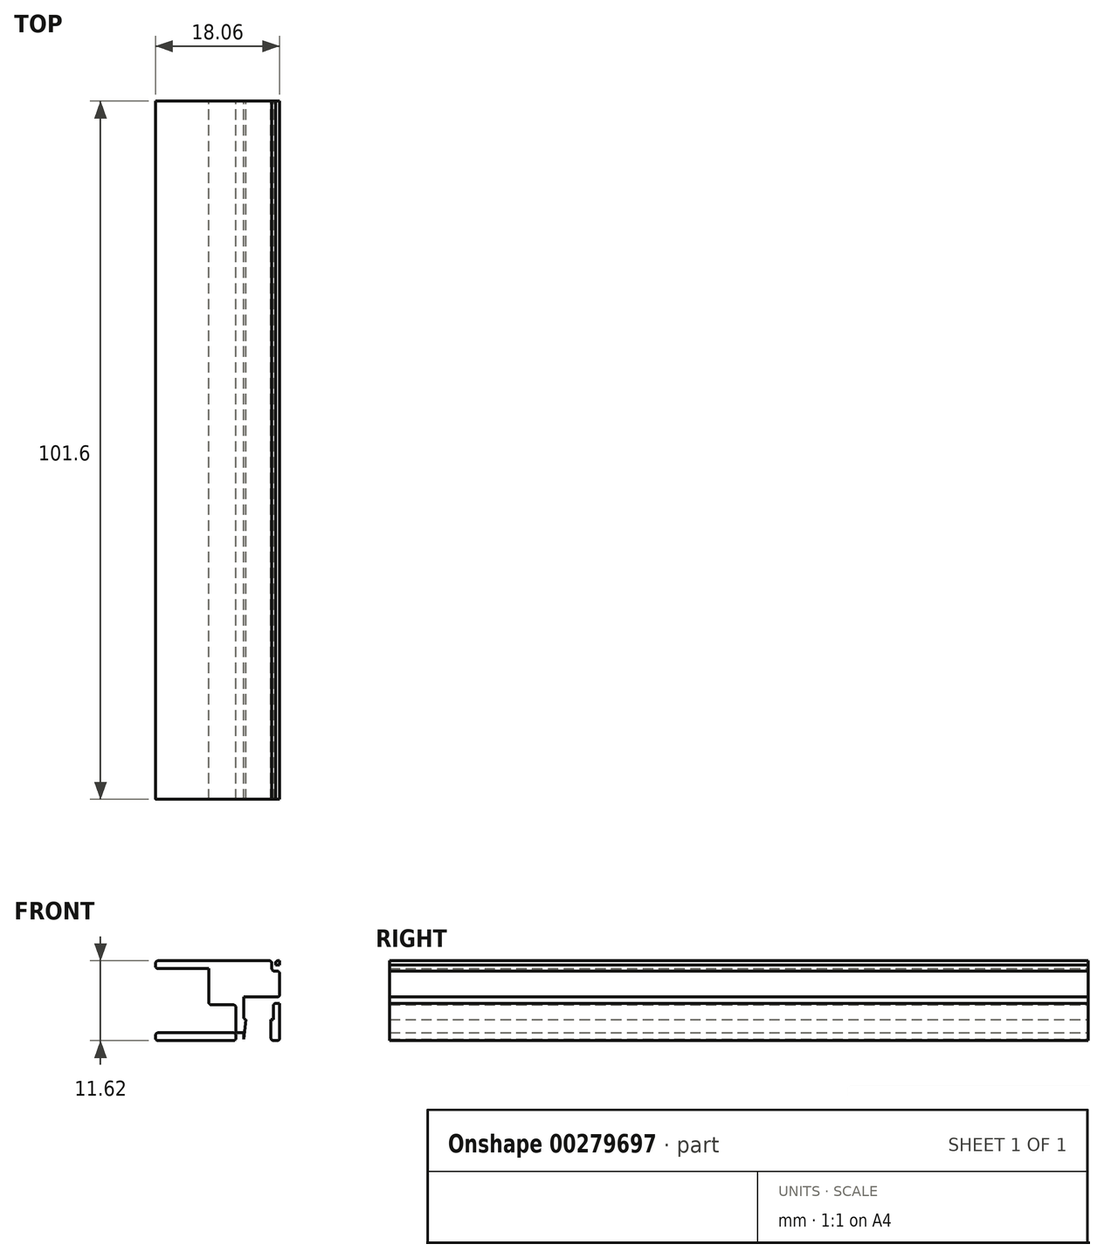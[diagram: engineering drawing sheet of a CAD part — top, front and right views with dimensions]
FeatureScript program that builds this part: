
annotation { "Feature Type Name" : "Feature", "Feature Type Description" : "" }
export const myFeature = defineFeature(function(context is Context, id is Id, definition is map)
    precondition{}
    {
        {
            var Q0;
            Q0=qCreatedBy(makeId("Front.planeOp"),FACE);
            var sketch = newSketch(context, id + "F0", { "sketchPlane" : qUnion([Q0])});
            skLineSegment(sketch, "E0.bottom", {"start": v(12.78, 5.81) * mm, "end": v(-12.78, 5.81) * mm});
            skLineSegment(sketch, "E0.top", {"start": v(12.78, -5.81) * mm, "end": v(-12.78, -5.81) * mm});
            skLineSegment(sketch, "E0.left", {"start": v(12.78, 5.81) * mm, "end": v(12.78, -5.81) * mm});
            skLineSegment(sketch, "E0.right", {"start": v(-12.78, 5.81) * mm, "end": v(-12.78, -5.81) * mm});
            skPoint(sketch, "E0.middle", {"position": v(0, 0) * mm});
            skLineSegment(sketch, "E1.bottom", {"start": v(-12.78, 5.81) * mm, "end": v(-6.43, 5.81) * mm});
            skLineSegment(sketch, "E1.top", {"start": v(-12.78, 4.67) * mm, "end": v(-6.43, 4.67) * mm});
            skLineSegment(sketch, "E1.left", {"start": v(-12.78, 5.81) * mm, "end": v(-12.78, 4.67) * mm});
            skLineSegment(sketch, "E1.right", {"start": v(-6.43, 5.81) * mm, "end": v(-6.43, 4.67) * mm});
            skLineSegment(sketch, "E2.bottom", {"start": v(-6.43, 5.81) * mm, "end": v(-5.28, 5.81) * mm});
            skLineSegment(sketch, "E2.top", {"start": v(-6.43, -5.81) * mm, "end": v(-5.28, -5.81) * mm});
            skLineSegment(sketch, "E2.left", {"start": v(-6.43, 5.81) * mm, "end": v(-6.43, -5.81) * mm});
            skLineSegment(sketch, "E2.right", {"start": v(-5.28, 5.81) * mm, "end": v(-5.28, -5.81) * mm});
            skLineSegment(sketch, "E3.bottom", {"start": v(-6.43, -5.81) * mm, "end": v(7.54, -5.81) * mm});
            skLineSegment(sketch, "E3.top", {"start": v(-6.43, -4.67) * mm, "end": v(7.54, -4.67) * mm});
            skLineSegment(sketch, "E3.left", {"start": v(-6.43, -5.81) * mm, "end": v(-6.43, -4.67) * mm});
            skLineSegment(sketch, "E3.right", {"start": v(7.54, -5.81) * mm, "end": v(7.54, -4.67) * mm});
            skLineSegment(sketch, "E4.bottom", {"start": v(7.54, -5.81) * mm, "end": v(6.4, -5.81) * mm});
            skLineSegment(sketch, "E4.top", {"start": v(7.54, 0.54) * mm, "end": v(6.4, 0.54) * mm});
            skLineSegment(sketch, "E4.left", {"start": v(7.54, -5.81) * mm, "end": v(7.54, 0.54) * mm});
            skLineSegment(sketch, "E4.right", {"start": v(6.4, -5.81) * mm, "end": v(6.4, 0.54) * mm});
            skLineSegment(sketch, "E5.bottom", {"start": v(7.54, 0.54) * mm, "end": v(1.32, 0.54) * mm});
            skLineSegment(sketch, "E5.top", {"start": v(7.54, -0.6) * mm, "end": v(1.32, -0.6) * mm});
            skLineSegment(sketch, "E5.left", {"start": v(7.54, 0.54) * mm, "end": v(7.54, -0.6) * mm});
            skLineSegment(sketch, "E5.right", {"start": v(1.32, 0.54) * mm, "end": v(1.32, -0.6) * mm});
            skLineSegment(sketch, "E6.bottom", {"start": v(1.32, -0.6) * mm, "end": v(2.46, -0.6) * mm});
            skLineSegment(sketch, "E6.top", {"start": v(1.96, 5.81) * mm, "end": v(2.46, 5.81) * mm});
            skLineSegment(sketch, "E7.bottom", {"start": v(2.46, 5.81) * mm, "end": v(-5.28, 5.81) * mm});
            skLineSegment(sketch, "E7.top", {"start": v(2.46, 4.67) * mm, "end": v(-5.28, 4.67) * mm});
            skLineSegment(sketch, "E7.left", {"start": v(2.46, 5.81) * mm, "end": v(2.46, 4.67) * mm});
            skLineSegment(sketch, "E7.right", {"start": v(-5.28, 5.81) * mm, "end": v(-5.28, 4.67) * mm});
            skLineSegment(sketch, "E8.left", {"start": v(6.4, 0.54) * mm, "end": v(6.4, 0.03) * mm});
            skLineSegment(sketch, "E9.bottom", {"start": v(6.4, 0.54) * mm, "end": v(12.78, 0.54) * mm});
            skLineSegment(sketch, "E9.top", {"start": v(6.4, -0.37) * mm, "end": v(12.78, -0.37) * mm});
            skLineSegment(sketch, "E9.left", {"start": v(6.4, 0.54) * mm, "end": v(6.4, -0.37) * mm});
            skLineSegment(sketch, "E9.right", {"start": v(12.78, 0.54) * mm, "end": v(12.78, -0.37) * mm});
            skLineSegment(sketch, "E10.bottom", {"start": v(12.78, -0.37) * mm, "end": v(11.86, -0.37) * mm});
            skLineSegment(sketch, "E10.top", {"start": v(12.78, -2.76) * mm, "end": v(11.86, -2.76) * mm});
            skLineSegment(sketch, "E10.left", {"start": v(12.78, -0.37) * mm, "end": v(12.78, -2.76) * mm});
            skLineSegment(sketch, "E10.right", {"start": v(11.86, -0.37) * mm, "end": v(11.86, -2.76) * mm});
            skLineSegment(sketch, "E11", {"start": v(12.78, -5.81) * mm, "end": v(11.5, -5.81) * mm});
            skLineSegment(sketch, "E12.bottom", {"start": v(12.78, 0.54) * mm, "end": v(11.63, 0.54) * mm});
            skLineSegment(sketch, "E12.top", {"start": v(12.78, 5.81) * mm, "end": v(11.63, 5.81) * mm});
            skLineSegment(sketch, "E12.left", {"start": v(12.78, 0.54) * mm, "end": v(12.78, 5.81) * mm});
            skLineSegment(sketch, "E12.right", {"start": v(11.63, 0.54) * mm, "end": v(11.63, 5.81) * mm});
            skLineSegment(sketch, "E13.top", {"start": v(12.78, -4.15) * mm, "end": v(11.5, -4.15) * mm});
            skLineSegment(sketch, "E13.left", {"start": v(12.78, -5.81) * mm, "end": v(12.78, -4.15) * mm});
            skLineSegment(sketch, "E13.right", {"start": v(11.5, -5.81) * mm, "end": v(11.5, -4.15) * mm});
            skArc(sketch, "E14", {"start": v(11.5, -4.15) * mm, "mid": v(12.14, -4.78) * mm, "end": v(12.78, -4.15) * mm});
            skLineSegment(sketch, "E15.bottom", {"start": v(12.78, 5.81) * mm, "end": v(12.15, 5.81) * mm});
            skLineSegment(sketch, "E15.top", {"start": v(12.78, 5.18) * mm, "end": v(12.15, 5.18) * mm});
            skLineSegment(sketch, "E15.left", {"start": v(12.78, 5.81) * mm, "end": v(12.78, 5.18) * mm});
            skLineSegment(sketch, "E15.right", {"start": v(12.15, 5.81) * mm, "end": v(12.15, 5.18) * mm});
            skCircle(sketch, "E16", {"center": v(12.15, 5.18) * mm, "radius": 0.89 * mm});
            skLineSegment(sketch, "E17.bottom", {"start": v(7.54, -0.6) * mm, "end": v(7.8, -0.6) * mm});
            skLineSegment(sketch, "E17.top", {"start": v(7.54, -0.37) * mm, "end": v(7.8, -0.37) * mm});
            skLineSegment(sketch, "E17.left", {"start": v(7.54, -0.37) * mm, "end": v(7.54, -0.6) * mm});
            skLineSegment(sketch, "E17.right", {"start": v(7.8, -0.37) * mm, "end": v(7.8, -0.6) * mm});
            skLineSegment(sketch, "E18", {"start": v(8.26, -0.37) * mm, "end": v(8.5, -0.37) * mm});
            skLineSegment(sketch, "E19.top", {"start": v(7.54, -0.63) * mm, "end": v(7.8, -0.63) * mm});
            skLineSegment(sketch, "E19.left", {"start": v(7.54, -0.37) * mm, "end": v(7.54, -0.63) * mm});
            skLineSegment(sketch, "E19.right", {"start": v(7.8, -0.37) * mm, "end": v(7.8, -0.63) * mm});
            skLineSegment(sketch, "E20", {"start": v(7.54, -0.63) * mm, "end": v(7.54, -0.88) * mm});
            skLineSegment(sketch, "E21", {"start": v(7.54, -1.4) * mm, "end": v(7.54, -1.64) * mm});
            skLineSegment(sketch, "E22", {"start": v(7.54, -1.64) * mm, "end": v(7.54, -1.9) * mm});
            skLineSegment(sketch, "E23", {"start": v(7.54, -1.9) * mm, "end": v(7.54, -2.15) * mm});
            skLineSegment(sketch, "E24", {"start": v(7.54, -2.15) * mm, "end": v(7.54, -2.4) * mm});
            skLineSegment(sketch, "E25", {"start": v(7.54, -2.4) * mm, "end": v(7.54, -2.66) * mm});
            skLineSegment(sketch, "E26", {"start": v(7.54, -2.66) * mm, "end": v(7.54, -4.67) * mm});
            skLineSegment(sketch, "E27", {"start": v(7.54, -0.88) * mm, "end": v(7.54, -1.14) * mm});
            skLineSegment(sketch, "E28", {"start": v(7.54, -2.66) * mm, "end": v(7.54, -2.91) * mm});
            skLineSegment(sketch, "E29", {"start": v(7.54, -3.17) * mm, "end": v(7.54, -3.42) * mm});
            skLineSegment(sketch, "E30", {"start": v(7.54, -3.42) * mm, "end": v(7.54, -3.68) * mm});
            skLineSegment(sketch, "E31", {"start": v(7.54, -3.68) * mm, "end": v(7.54, -3.93) * mm});
            skLineSegment(sketch, "E32", {"start": v(7.54, -3.93) * mm, "end": v(7.54, -4.18) * mm});
            skLineSegment(sketch, "E33", {"start": v(7.54, -3) * mm, "end": v(7.54, -5.81) * mm});
            skLineSegment(sketch, "E34.bottom", {"start": v(12.78, -2.76) * mm, "end": v(11.5, -2.76) * mm});
            skLineSegment(sketch, "E34.left", {"start": v(12.78, -2.76) * mm, "end": v(12.78, -4.15) * mm});
            skLineSegment(sketch, "E34.right", {"start": v(11.5, -2.76) * mm, "end": v(11.5, -4.15) * mm});
            skLineSegment(sketch, "E35", {"start": v(7.54, -5.58) * mm, "end": v(7.87, -2.76) * mm});
            skLineSegment(sketch, "E36", {"start": v(7.87, -2.76) * mm, "end": v(7.54, -2.76) * mm});
            skLineSegment(sketch, "E37", {"start": v(7.54, -2.76) * mm, "end": v(7.54, -5.58) * mm});
            skLineSegment(sketch, "E38.bottom", {"start": v(2.46, 5.81) * mm, "end": v(1.32, 5.81) * mm});
            skLineSegment(sketch, "E38.top", {"start": v(2.46, -0.6) * mm, "end": v(1.32, -0.6) * mm});
            skLineSegment(sketch, "E38.left", {"start": v(2.46, 5.81) * mm, "end": v(2.46, -0.6) * mm});
            skLineSegment(sketch, "E38.right", {"start": v(1.32, 5.81) * mm, "end": v(1.32, -0.6) * mm});
            skSolve(sketch);
        }
        {
            var Q0;
            {var subQ0=sQuery(id+"F0.wireOp",EDGE,"E1.bottom");Q0=makeQuery(id+"F0.imprint","IMPRINT",FACE,{"disambiguationData":[TD([[makeQuery(id+"F0.imprint","IMPRINT",EDGE,{"derivedFrom":subQ0}),-1.0]])]});}
            var Q1;
            {var subQ5=sQuery(id+"F0.wireOp",EDGE,"E7.right");Q1=makeQuery(id+"F0.imprint","IMPRINT",FACE,{"disambiguationData":[TD([[makeQuery(id+"F0.imprint","IMPRINT",EDGE,{"derivedFrom":subQ5}),1.0]])]});}
            var Q2;
            {var subQ7=sQuery(id+"F0.wireOp",EDGE,"E2.bottom");Q2=makeQuery(id+"F0.imprint","IMPRINT",FACE,{"disambiguationData":[TD([[makeQuery(id+"F0.imprint","IMPRINT",EDGE,{"derivedFrom":subQ7}),-1.0]])]});}
            var Q3;
            {var subQ5=sQuery(id+"F0.wireOp",EDGE,"E7.left");Q3=makeQuery(id+"F0.imprint","IMPRINT",FACE,{"disambiguationData":[TD([[makeQuery(id+"F0.imprint","IMPRINT",EDGE,{"derivedFrom":subQ5}),-1.0]])]});}
            var Q4;
            {var subQ0=sQuery(id+"F0.wireOp",EDGE,"E6.left");var subQ1=sQuery(id+"F0.wireOp",EDGE,"E5.bottom");var subQ2=makeQuery(id+"F0.imprint","INTERSECT",VERTEX,{"derivedFrom":[subQ1,subQ0]});Q4=makeQuery(id+"F0.imprint","IMPRINT",FACE,{"disambiguationData":[TD([[makeQuery(id+"F0.imprint","IMPRINT",EDGE,{"disambiguationData":[TD([[subQ2,1.0]])],"derivedFrom":subQ1}),-1.0]])]});}
            var Q5;
            {var subQ5=sQuery(id+"F0.wireOp",EDGE,"E6.bottom");Q5=makeQuery(id+"F0.imprint","IMPRINT",FACE,{"disambiguationData":[TD([[makeQuery(id+"F0.imprint","IMPRINT",EDGE,{"derivedFrom":subQ5}),1.0]])]});}
            var Q6;
            {var subQ5=sQuery(id+"F0.wireOp",EDGE,"E3.left");Q6=makeQuery(id+"F0.imprint","IMPRINT",FACE,{"disambiguationData":[TD([[makeQuery(id+"F0.imprint","IMPRINT",EDGE,{"derivedFrom":subQ5}),-1.0]])]});}
            var Q7;
            {var subQ0=sQuery(id+"F0.wireOp",EDGE,"E3.bottom");var subQ1=sQuery(id+"F0.wireOp",EDGE,"E2.right");var subQ2=makeQuery(id+"F0.imprint","INTERSECT",VERTEX,{"derivedFrom":[subQ1,subQ0]});Q7=makeQuery(id+"F0.imprint","IMPRINT",FACE,{"disambiguationData":[TD([[makeQuery(id+"F0.imprint","IMPRINT",EDGE,{"disambiguationData":[TD([[subQ2,1.0]])],"derivedFrom":subQ1}),1.0]])]});}
            var Q8;
            {var subQ5=sQuery(id+"F0.wireOp",EDGE,"E4.bottom");Q8=makeQuery(id+"F0.imprint","IMPRINT",FACE,{"disambiguationData":[TD([[makeQuery(id+"F0.imprint","IMPRINT",EDGE,{"derivedFrom":subQ5}),-1.0]])]});}
            var Q9;
            {var subQ1=sQuery(id+"F0.wireOp",EDGE,"E5.bottom");var subQ3=sQuery(id+"F0.wireOp",EDGE,"E6.right");var subQ4=makeQuery(id+"F0.imprint","INTERSECT",VERTEX,{"derivedFrom":[subQ1,subQ3]});Q9=makeQuery(id+"F0.imprint","IMPRINT",FACE,{"disambiguationData":[TD([[makeQuery(id+"F0.imprint","IMPRINT",EDGE,{"disambiguationData":[TD([[subQ4,1.0]])],"derivedFrom":subQ1}),1.0]])]});}
            var Q10;
            {var subQ0=sQuery(id+"F0.wireOp",EDGE,"E5.left");Q10=makeQuery(id+"F0.imprint","IMPRINT",FACE,{"disambiguationData":[TD([[makeQuery(id+"F0.imprint","IMPRINT",EDGE,{"derivedFrom":subQ0}),-1.0]])]});}
            var Q11;
            {var subQ0=sQuery(id+"F0.wireOp",EDGE,"E4.left");var subQ1=sQuery(id+"F0.wireOp",EDGE,"E3.top");var subQ2=makeQuery(id+"F0.imprint","INTERSECT",VERTEX,{"derivedFrom":[subQ1,subQ0]});Q11=makeQuery(id+"F0.imprint","IMPRINT",FACE,{"disambiguationData":[TD([[makeQuery(id+"F0.imprint","IMPRINT",EDGE,{"disambiguationData":[TD([[subQ2,1.0]])],"derivedFrom":subQ1}),1.0]])]});}
            var Q12;
            {var subQ1=sQuery(id+"F0.wireOp",EDGE,"E4.left");var subQ3=sQuery(id+"F0.wireOp",EDGE,"E9.top");var subQ4=makeQuery(id+"F0.imprint","INTERSECT",VERTEX,{"derivedFrom":[subQ1,subQ3]});Q12=makeQuery(id+"F0.imprint","IMPRINT",FACE,{"disambiguationData":[TD([[makeQuery(id+"F0.imprint","IMPRINT",EDGE,{"disambiguationData":[TD([[subQ4,-1.0]])],"derivedFrom":subQ1}),1.0]])]});}
            var Q13;
            {var subQ5=sQuery(id+"F0.wireOp",EDGE,"E5.left");Q13=makeQuery(id+"F0.imprint","IMPRINT",FACE,{"disambiguationData":[TD([[makeQuery(id+"F0.imprint","IMPRINT",EDGE,{"derivedFrom":subQ5}),1.0]])]});}
            var Q14;
            {var subQ0=sQuery(id+"F0.wireOp",EDGE,"E12.bottom");Q14=makeQuery(id+"F0.imprint","IMPRINT",FACE,{"disambiguationData":[TD([[makeQuery(id+"F0.imprint","IMPRINT",EDGE,{"derivedFrom":subQ0}),-1.0]])]});}
            var Q15;
            {var subQ5=sQuery(id+"F0.wireOp",EDGE,"E12.top");Q15=makeQuery(id+"F0.imprint","IMPRINT",FACE,{"disambiguationData":[TD([[makeQuery(id+"F0.imprint","IMPRINT",EDGE,{"derivedFrom":subQ5}),1.0]])]});}
            var Q16;
            {var subQ1=sQuery(id+"F0.wireOp",EDGE,"E0.bottom");var subQ3=sQuery(id+"F0.wireOp",EDGE,"E16");var subQ4=makeQuery(id+"F0.imprint","INTERSECT",VERTEX,{"derivedFrom":[subQ1,subQ3]});Q16=makeQuery(id+"F0.imprint","IMPRINT",FACE,{"disambiguationData":[TD([[makeQuery(id+"F0.imprint","IMPRINT",EDGE,{"disambiguationData":[TD([[subQ4,-1.0]])],"derivedFrom":subQ3}),1.0]])]});}
            var Q17;
            Q17=makeQuery(id+"F0.imprint","IMPRINT",FACE,{"disambiguationData":[TD([[makeQuery(id+"F0.imprint","IMPRINT",EDGE,{"derivedFrom":sQuery(id+"F0.wireOp",EDGE,"E15.bottom")}),1.0]])]});
            var Q18;
            {var subQ0=sQuery(id+"F0.wireOp",EDGE,"E12.top");Q18=makeQuery(id+"F0.imprint","IMPRINT",FACE,{"disambiguationData":[TD([[makeQuery(id+"F0.imprint","IMPRINT",EDGE,{"derivedFrom":subQ0}),-1.0]])]});}
            var Q19;
            Q19=makeQuery(id+"F0.imprint","IMPRINT",FACE,{"disambiguationData":[TD([[makeQuery(id+"F0.imprint","IMPRINT",EDGE,{"derivedFrom":sQuery(id+"F0.wireOp",EDGE,"E10.bottom")}),1.0]])]});
            var Q20;
            Q20=makeQuery(id+"F0.imprint","IMPRINT",FACE,{"disambiguationData":[TD([[makeQuery(id+"F0.imprint","IMPRINT",EDGE,{"derivedFrom":sQuery(id+"F0.wireOp",EDGE,"E0.left")}),-1.0]])]});
            var Q21;
            {var subQ0=sQuery(id+"F0.wireOp",EDGE,"E13.top");Q21=makeQuery(id+"F0.imprint","IMPRINT",FACE,{"disambiguationData":[TD([[makeQuery(id+"F0.imprint","IMPRINT",EDGE,{"derivedFrom":subQ0}),1.0]])]});}
            var Q22;
            {var subQ0=sQuery(id+"F0.wireOp",EDGE,"E17.left");Q22=makeQuery(id+"F0.imprint","IMPRINT",FACE,{"disambiguationData":[TD([[makeQuery(id+"F0.imprint","IMPRINT",EDGE,{"derivedFrom":subQ0}),-1.0]])]});}
            var Q23;
            Q23=makeQuery(id+"F0.imprint","IMPRINT",FACE,{"disambiguationData":[TD([[makeQuery(id+"F0.imprint","IMPRINT",EDGE,{"derivedFrom":sQuery(id+"F0.wireOp",EDGE,"E13.top")}),-1.0]])]});
            var Q24;
            Q24=makeQuery(id+"F0.imprint","IMPRINT",FACE,{"disambiguationData":[TD([[makeQuery(id+"F0.imprint","IMPRINT",EDGE,{"derivedFrom":sQuery(id+"F0.wireOp",EDGE,"E14")}),1.0]])]});
            var Q25;
            {var subQ4=sQuery(id+"F0.wireOp",EDGE,"9RvwCQEr-Ok0x-Px2Q-7vT0-DrrcIIfK4BPZ");Q25=makeQuery(id+"F0.imprint","IMPRINT",FACE,{"disambiguationData":[TD([[makeQuery(id+"F0.imprint","IMPRINT",EDGE,{"derivedFrom":subQ4}),1.0]])]});}
            var Q26;
            {var subQ4=sQuery(id+"F0.wireOp",EDGE,"E35");Q26=makeQuery(id+"F0.imprint","IMPRINT",FACE,{"disambiguationData":[TD([[makeQuery(id+"F0.imprint","IMPRINT",EDGE,{"derivedFrom":subQ4}),1.0]])]});}
            var Q27;
            {var subQ0=sQuery(id+"F0.wireOp",EDGE,"E38.left");var subQ1=sQuery(id+"F0.wireOp",EDGE,"E7.top");var subQ2=makeQuery(id+"F0.imprint","INTERSECT",VERTEX,{"derivedFrom":[subQ1,subQ0]});Q27=makeQuery(id+"F0.imprint","IMPRINT",FACE,{"disambiguationData":[TD([[makeQuery(id+"F0.imprint","IMPRINT",EDGE,{"disambiguationData":[TD([[subQ2,-1.0]])],"derivedFrom":subQ1}),-1.0]])]});}
            var Q28;
            {var subQ5=sQuery(id+"F0.wireOp",EDGE,"E9.left");var subQ8=makeQuery(id+"F0.imprint","IMPRINT",VERTEX,{"derivedFrom":subQ5});Q28=makeQuery(id+"F0.imprint","IMPRINT",FACE,{"disambiguationData":[TD([[makeQuery(id+"F0.imprint","IMPRINT",EDGE,{"disambiguationData":[TD([[subQ8,1.0]])],"derivedFrom":subQ5}),-1.0]])]});}
            var Q29;
            {var subQ1=sQuery(id+"F0.wireOp",EDGE,"E4.right");var subQ3=sQuery(id+"F0.wireOp",EDGE,"E5.top");var subQ4=makeQuery(id+"F0.imprint","INTERSECT",VERTEX,{"derivedFrom":[subQ1,subQ3]});Q29=makeQuery(id+"F0.imprint","IMPRINT",FACE,{"disambiguationData":[TD([[makeQuery(id+"F0.imprint","IMPRINT",EDGE,{"disambiguationData":[TD([[subQ4,-1.0]])],"derivedFrom":subQ1}),-1.0]])]});}
            extrude(context, id + "F1", {"entities" : qUnion([Q0, Q1, Q2, Q3, Q4, Q5, Q6, Q7, Q8, Q9, Q10, Q11, Q12, Q13, Q14, Q15, Q16, Q17, Q18, Q19, Q20, Q21, Q22, Q23, Q24, Q25, Q26, Q27, Q28, Q29]), "endBound" : BoundingType.SYMMETRIC, "depth" : 101.6 * mm, "offsetDistance" : 25.4 * mm});
        }
        {
            var Q0;
            Q0=makeQuery(id+"F1.opExtrude","SWEPT_EDGE",EDGE,{"disambiguationData":[OSD([sQuery(id+"F0.wireOp",EDGE,"E1.bottom"),sQuery(id+"F0.wireOp",EDGE,"E1.left")])]});
            var Q1;
            Q1=makeQuery(id+"F1.opExtrude","SWEPT_EDGE",EDGE,{"disambiguationData":[OSD([sQuery(id+"F0.wireOp",EDGE,"E0.right"),sQuery(id+"F0.wireOp",EDGE,"E1.top"),sQuery(id+"F0.wireOp",EDGE,"E1.left")])]});
            var Q2;
            Q2=makeQuery(id+"F1.opExtrude","SWEPT_EDGE",EDGE,{"disambiguationData":[OSD([sQuery(id+"F0.wireOp",EDGE,"E1.top"),sQuery(id+"F0.wireOp",EDGE,"E2.left")])]});
            var Q3;
            Q3=makeQuery(id+"F1.opExtrude","SWEPT_EDGE",EDGE,{"disambiguationData":[OSD([sQuery(id+"F0.wireOp",EDGE,"E0.top"),sQuery(id+"F0.wireOp",EDGE,"E3.bottom"),sQuery(id+"F0.wireOp",EDGE,"E3.left")])]});
            var Q4;
            Q4=makeQuery(id+"F1.opExtrude","SWEPT_EDGE",EDGE,{"disambiguationData":[OSD([sQuery(id+"F0.wireOp",EDGE,"E5.top"),sQuery(id+"F0.wireOp",EDGE,"E9.left")])]});
            var Q5;
            Q5=makeQuery(id+"F1.opExtrude","SWEPT_EDGE",EDGE,{"disambiguationData":[OSD([sQuery(id+"F0.wireOp",EDGE,"E3.top"),sQuery(id+"F0.wireOp",EDGE,"E4.right")])]});
            var Q6;
            Q6=makeQuery(id+"F1.opExtrude","SWEPT_EDGE",EDGE,{"disambiguationData":[OSD([sQuery(id+"F0.wireOp",EDGE,"E6.bottom"),sQuery(id+"F0.wireOp",EDGE,"E6.left")])]});
            var Q7;
            Q7=makeQuery(id+"F1.opExtrude","SWEPT_EDGE",EDGE,{"disambiguationData":[OSD([sQuery(id+"F0.wireOp",EDGE,"E6.left"),sQuery(id+"F0.wireOp",EDGE,"E7.top")])]});
            var Q8;
            Q8=makeQuery(id+"F1.opExtrude","SWEPT_EDGE",EDGE,{"disambiguationData":[OSD([sQuery(id+"F0.wireOp",EDGE,"E2.right"),sQuery(id+"F0.wireOp",EDGE,"E7.top"),sQuery(id+"F0.wireOp",EDGE,"E7.right")])]});
            var Q9;
            Q9=makeQuery(id+"F1.opExtrude","SWEPT_EDGE",EDGE,{"disambiguationData":[OSD([sQuery(id+"F0.wireOp",EDGE,"E2.right"),sQuery(id+"F0.wireOp",EDGE,"E3.top")])]});
            var Q10;
            Q10=makeQuery(id+"F1.opExtrude","SWEPT_EDGE",EDGE,{"disambiguationData":[OSD([sQuery(id+"F0.wireOp",EDGE,"E0.top"),sQuery(id+"F0.wireOp",EDGE,"E4.bottom"),sQuery(id+"F0.wireOp",EDGE,"E4.left")])]});
            var Q11;
            Q11=makeQuery(id+"F1.opExtrude","SWEPT_EDGE",EDGE,{"disambiguationData":[OSD([sQuery(id+"F0.wireOp",EDGE,"E9.top"),sQuery(id+"F0.wireOp",EDGE,"E10.bottom"),sQuery(id+"F0.wireOp",EDGE,"E10.right")])]});
            var Q12;
            Q12=makeQuery(id+"F1.opExtrude","SWEPT_EDGE",EDGE,{"disambiguationData":[OSD([sQuery(id+"F0.wireOp",EDGE,"r4VEyfAt-ehJe-geew-MrV4-AbPzkRhEMfo9"),sQuery(id+"F0.wireOp",EDGE,"Kfbqsl1S-sgpj-Rs7s-NmJZ-xIiJlLXwGIcJ")])]});
            var Q13;
            Q13=makeQuery(id+"F1.opExtrude","SWEPT_EDGE",EDGE,{"disambiguationData":[OSD([sQuery(id+"F0.wireOp",EDGE,"E15.bottom"),sQuery(id+"F0.wireOp",EDGE,"E15.left"),sQuery(id+"F0.wireOp",EDGE,"E16")])]});
            var Q14;
            Q14=makeQuery(id+"F1.opExtrude","SWEPT_EDGE",EDGE,{"disambiguationData":[OSD([sQuery(id+"F0.wireOp",EDGE,"E5.bottom"),sQuery(id+"F0.wireOp",EDGE,"E6.right")])]});
            var Q15;
            Q15=makeQuery(id+"F1.opExtrude","SWEPT_EDGE",EDGE,{"disambiguationData":[OSD([sQuery(id+"F0.wireOp",EDGE,"E0.bottom"),sQuery(id+"F0.wireOp",EDGE,"E7.bottom"),sQuery(id+"F0.wireOp",EDGE,"E7.left")])]});
            var Q16;
            Q16=makeQuery(id+"F1.opExtrude","SWEPT_EDGE",EDGE,{"disambiguationData":[OSD([sQuery(id+"F0.wireOp",EDGE,"E9.bottom"),sQuery(id+"F0.wireOp",EDGE,"E12.bottom"),sQuery(id+"F0.wireOp",EDGE,"E12.right")])]});
            var Q17;
            Q17=makeQuery(id+"F1.opExtrude","SWEPT_EDGE",EDGE,{"disambiguationData":[OSD([sQuery(id+"F0.wireOp",EDGE,"E12.right"),sQuery(id+"F0.wireOp",EDGE,"E16")])]});
            var Q18;
            Q18=makeQuery(id+"F1.opExtrude","SWEPT_EDGE",EDGE,{"disambiguationData":[OSD([sQuery(id+"F0.wireOp",EDGE,"E38.top"),sQuery(id+"F0.wireOp",EDGE,"E38.right")])]});
            fillet(context, id + "F2", {"entities" : qUnion([Q0, Q1, Q2, Q3, Q4, Q5, Q6, Q7, Q8, Q9, Q10, Q11, Q12, Q13, Q14, Q15, Q16, Q17, Q18]), "radius" : 0.38 * mm, "tangentPropagation" : true, "allowEdgeOverflow" : false});
        }
    });
